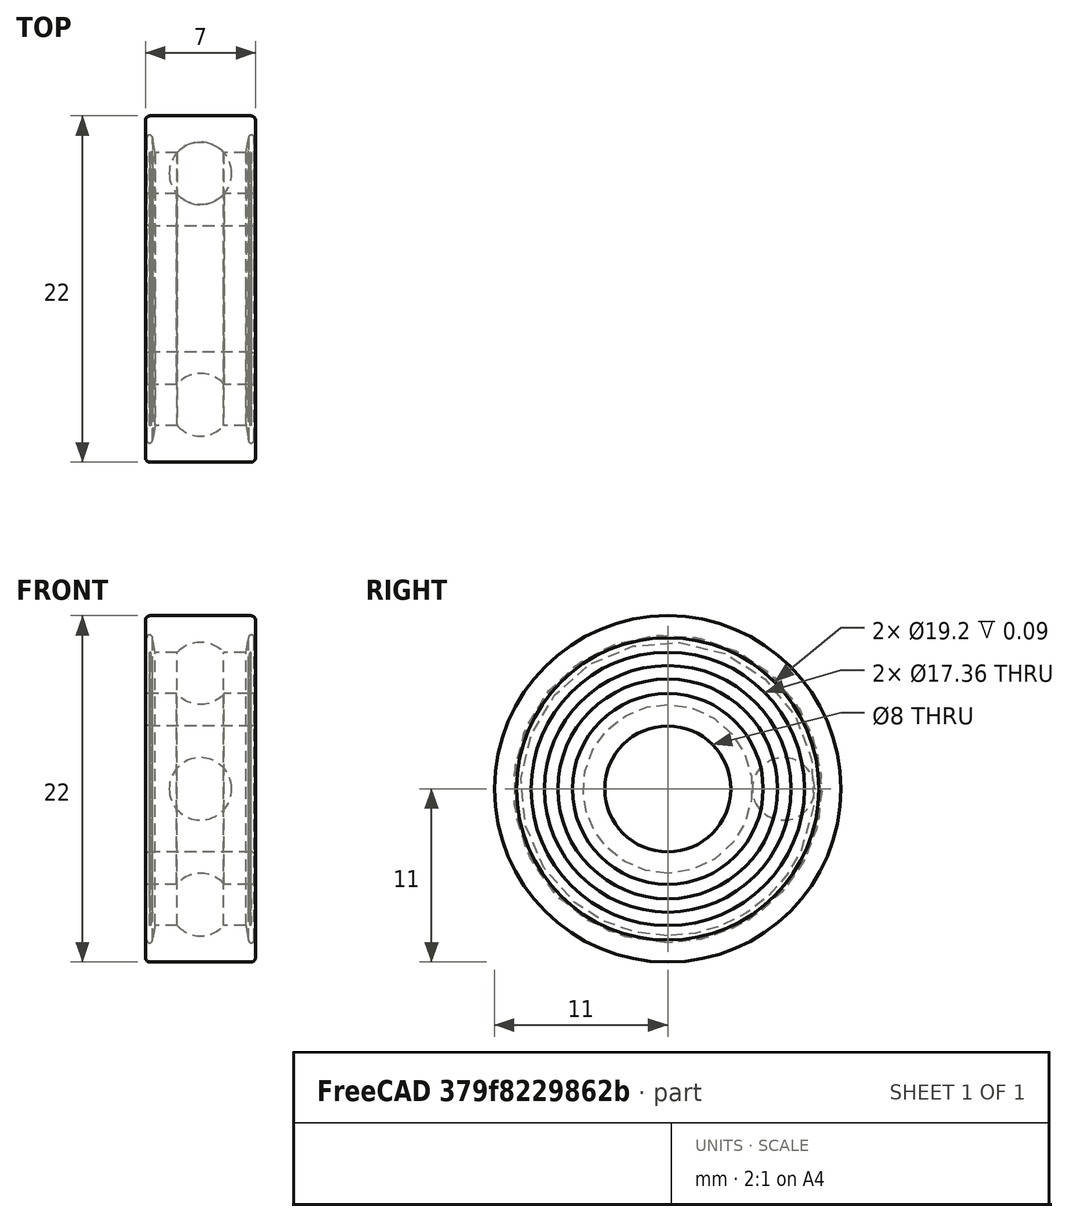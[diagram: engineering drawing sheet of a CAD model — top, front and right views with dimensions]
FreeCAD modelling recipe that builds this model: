
FCSTD DOCUMENT  (FreeCAD 2020.10.16R22739 +2665 (Git))
Label: lozysko 608
License: All rights reserved
LicenseURL: http://en.wikipedia.org/wiki/All_rights_reserved
objects: App::Link×12, Part::Feature×4, Part::FeaturePython×4, App::FeaturePython×2
note: 7 computed .brp shape members not serialized (recipe doc carries the construction recipe); baked Part::Feature solids carry a one-line shape summary decoded from their .brp

FEATURE [Part::Feature] Solid  label="_608-2RSH_PART1"
  shape: bbox 7 x 17.36 x 17.36 mm, 26 faces (baked)
FEATURE [Part::Feature] Solid001  label="_608-2RSH_PART2"
  shape: bbox 7 x 23.81 x 23.81 mm, 14 faces (baked)
FEATURE [Part::Feature] Solid002  label="_608-2RSH_PART3"
  shape: bbox 3.969 x 3.969 x 3.969 mm, 1 faces (baked)
FEATURE [App::Link] Link  label="_608-2RSH_PART004"
  LinkPlacement = pos=(0,0,0) rot=(-1,0,0;0.897598rad)
  LinkedObject = -> Solid002
  Placement = pos=(0,0,0) rot=(-1,0,0;0.897598rad)
  SyncGroupVisibility = false
  _LinkVersion = 1
FEATURE [App::Link] Link001  label="_608-2RSH_PART005"
  LinkPlacement = pos=(0,0,0) rot=(-1,0,0;1.7952rad)
  LinkedObject = -> Solid002
  Placement = pos=(0,0,0) rot=(-1,0,0;1.7952rad)
  SyncGroupVisibility = false
  _LinkVersion = 1
FEATURE [App::Link] Link002  label="_608-2RSH_PART006"
  LinkPlacement = pos=(0,0,0) rot=(1,0,0;3.59039rad)
  LinkedObject = -> Solid002
  Placement = pos=(0,0,0) rot=(1,0,0;3.59039rad)
  SyncGroupVisibility = false
  _LinkVersion = 1
FEATURE [App::Link] Link003  label="_608-2RSH_PART007"
  LinkPlacement = pos=(0,0,0) rot=(1,0,0;2.69279rad)
  LinkedObject = -> Solid002
  Placement = pos=(0,0,0) rot=(1,0,0;2.69279rad)
  SyncGroupVisibility = false
  _LinkVersion = 1
FEATURE [App::Link] Link004  label="_608-2RSH_PART008"
  LinkPlacement = pos=(0,0,0) rot=(1,0,0;1.7952rad)
  LinkedObject = -> Solid002
  Placement = pos=(0,0,0) rot=(1,0,0;1.7952rad)
  SyncGroupVisibility = false
  _LinkVersion = 1
FEATURE [App::Link] Link005  label="_608-2RSH_PART009"
  LinkPlacement = pos=(0,0,0) rot=(1,0,0;0.897598rad)
  LinkedObject = -> Solid002
  Placement = pos=(0,0,0) rot=(1,0,0;0.897598rad)
  SyncGroupVisibility = false
  _LinkVersion = 1
FEATURE [Part::Feature] Compound  label="_608-2RSH_PART4"
  shape: bbox 2e-07 x 2e-07 x 2e-07 mm, 0 faces, 0 solids (baked)
FEATURE [App::Link] Link006  label="_608-2RSH_PART010"
  LinkPlacement = pos=(0,0,0) rot=(-1,0,0;0.897598rad)
  LinkedObject = -> Compound
  Placement = pos=(0,0,0) rot=(-1,0,0;0.897598rad)
  SyncGroupVisibility = false
  _LinkVersion = 1
FEATURE [App::Link] Link007  label="_608-2RSH_PART011"
  LinkPlacement = pos=(0,0,0) rot=(-1,0,0;1.7952rad)
  LinkedObject = -> Compound
  Placement = pos=(0,0,0) rot=(-1,0,0;1.7952rad)
  SyncGroupVisibility = false
  _LinkVersion = 1
FEATURE [App::Link] Link008  label="_608-2RSH_PART012"
  LinkPlacement = pos=(0,0,0) rot=(1,0,0;3.59039rad)
  LinkedObject = -> Compound
  Placement = pos=(0,0,0) rot=(1,0,0;3.59039rad)
  SyncGroupVisibility = false
  _LinkVersion = 1
FEATURE [App::Link] Link009  label="_608-2RSH_PART013"
  LinkPlacement = pos=(0,0,0) rot=(1,0,0;2.69279rad)
  LinkedObject = -> Compound
  Placement = pos=(0,0,0) rot=(1,0,0;2.69279rad)
  SyncGroupVisibility = false
  _LinkVersion = 1
FEATURE [App::Link] Link010  label="_608-2RSH_PART014"
  LinkPlacement = pos=(0,0,0) rot=(1,0,0;1.7952rad)
  LinkedObject = -> Compound
  Placement = pos=(0,0,0) rot=(1,0,0;1.7952rad)
  SyncGroupVisibility = false
  _LinkVersion = 1
FEATURE [App::Link] Link011  label="_608-2RSH_PART015"
  LinkPlacement = pos=(0,0,0) rot=(1,0,0;0.897598rad)
  LinkedObject = -> Compound
  Placement = pos=(0,0,0) rot=(1,0,0;0.897598rad)
  SyncGroupVisibility = false
  _LinkVersion = 1
FEATURE [App::FeaturePython] Constraints  # WARN: FeaturePython — macro-defined, semantics opaque (R4)
  _LinkVersion = 1
  _Version = 1
FEATURE [Part::FeaturePython] Parts  # WARN: FeaturePython — macro-defined, semantics opaque (R4)
  Group = -> [Solid,Solid001,Solid002,Link,Link001,Link002,Link003,Link004,Link005,Compound,Link006,Link007,Link008,Link009,Link010,Link011]
  GroupMode = 0
  _LinkVersion = 1
FEATURE [Part::FeaturePython] Assembly  label="608-2RS"  # WARN: FeaturePython — macro-defined, semantics opaque (R4)
  AutoRelax = true
  BuildShape = 0
  Freeze = false
  Group = -> [Constraints,Elements,Parts]
  Verbose = false
  _LinkVersion = 1
  _SolverType = 1
  _Version = 1
FEATURE [App::FeaturePython] Elements  # WARN: FeaturePython — macro-defined, semantics opaque (R4)
  Group = -> [Element,Element001]
  _LinkVersion = 1
FEATURE [Part::FeaturePython] Element  # link proxy (typed FeaturePython)
  Detach = false
  LinkTransform = true
  LinkedObject = -> Solid [Face11]
  _LinkVersion = 1
  _Parent = -> Elements
FEATURE [Part::FeaturePython] Element001  # link proxy (typed FeaturePython)
  Detach = false
  LinkTransform = true
  LinkedObject = -> Compound [Vertex1]
  _LinkVersion = 1
  _Parent = -> Elements
